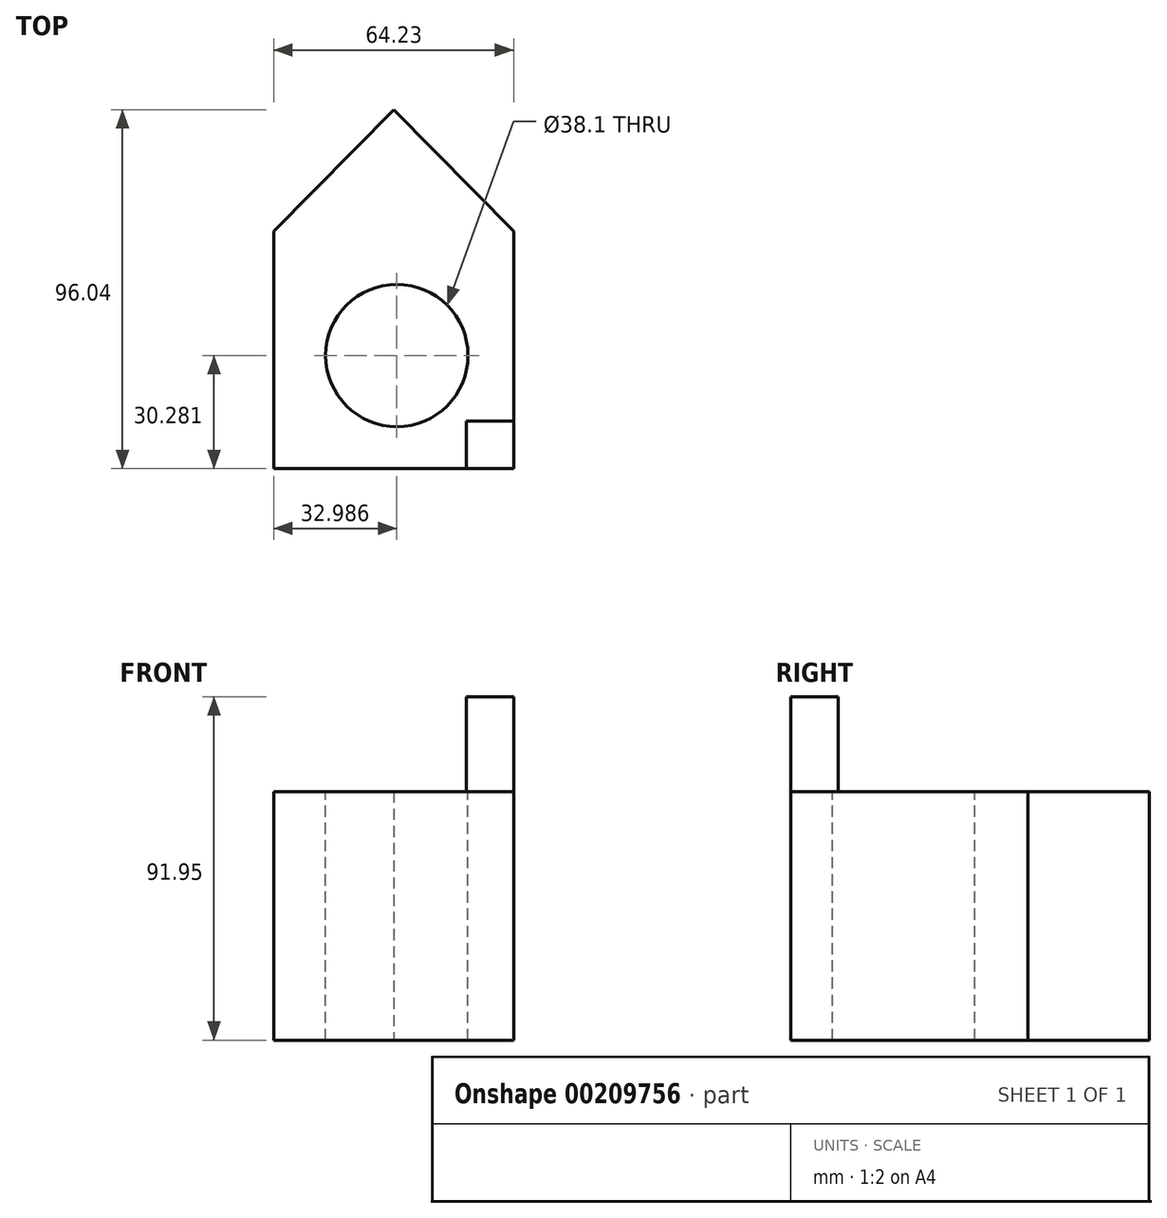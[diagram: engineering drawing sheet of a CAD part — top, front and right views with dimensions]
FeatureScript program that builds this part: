
annotation { "Feature Type Name" : "Feature", "Feature Type Description" : "" }
export const myFeature = defineFeature(function(context is Context, id is Id, definition is map)
    precondition{}
    {
        {
            var Q0;
            Q0=qCreatedBy(makeId("Top.planeOp"),FACE);
            var sketch = newSketch(context, id + "F0", { "sketchPlane" : qUnion([Q0])});
            skLineSegment(sketch, "E0.bottom", {"start": v(0, 0) * mm, "end": v(64.23, 0) * mm});
            skLineSegment(sketch, "E0.top", {"start": v(0, 63.5) * mm, "end": v(64.23, 63.5) * mm});
            skLineSegment(sketch, "E0.left", {"start": v(0, 0) * mm, "end": v(0, 63.5) * mm});
            skLineSegment(sketch, "E0.right", {"start": v(64.23, 0) * mm, "end": v(64.23, 63.5) * mm});
            skLineSegment(sketch, "E1", {"start": v(0, 63.5) * mm, "end": v(32.12, 96.04) * mm});
            skPoint(sketch, "E1.endSnap0", {"position": v(32.12, 63.5) * mm});
            skLineSegment(sketch, "E2", {"start": v(64.23, 63.5) * mm, "end": v(32.12, 96.04) * mm});
            skSolve(sketch);
        }
        {
            var Q0;
            Q0 = qSketchRegion(id + "F0", true);
            extrude(context, id + "F1", {"entities" : qUnion([Q0]), "depth" : 66.55 * mm});
        }
        {
            var Q0;
            Q0=makeQuery(id+"F1.opExtrude","CAP_FACE",FACE,{"disambiguationData":[OSD([sQuery(id+"F0.wireOp",EDGE,"E0.bottom"),sQuery(id+"F0.wireOp",EDGE,"E0.left"),sQuery(id+"F0.wireOp",EDGE,"E0.right"),sQuery(id+"F0.wireOp",EDGE,"E1"),sQuery(id+"F0.wireOp",EDGE,"E2")])],"isStart":false});
            var sketch = newSketch(context, id + "F2", { "sketchPlane" : qUnion([Q0])});
            skCircle(sketch, "E3", {"center": v(32.99, 30.28) * mm, "radius": 19.05 * mm});
            skSolve(sketch);
        }
        {
            var Q0;
            Q0 = qSketchRegion(id + "F2", true);
            extrude(context, id + "F3", {"entities" : qUnion([Q0]), "operationType" : NewBodyOperationType.REMOVE, "endBound" : BoundingType.THROUGH_ALL, "oppositeDirection" : true, "depth" : 25.4 * mm});
        }
        {
            var Q0;
            Q0=makeQuery(id+"F1.opExtrude","CAP_FACE",FACE,{"disambiguationData":[OSD([sQuery(id+"F0.wireOp",EDGE,"E0.bottom"),sQuery(id+"F0.wireOp",EDGE,"E0.left"),sQuery(id+"F0.wireOp",EDGE,"E0.right"),sQuery(id+"F0.wireOp",EDGE,"E1"),sQuery(id+"F0.wireOp",EDGE,"E2")])],"isStart":false});
            var sketch = newSketch(context, id + "F4", { "sketchPlane" : qUnion([Q0])});
            skLineSegment(sketch, "E4.bottom", {"start": v(51.53, 12.7) * mm, "end": v(64.23, 12.7) * mm});
            skLineSegment(sketch, "E4.top", {"start": v(51.53, 0) * mm, "end": v(64.23, 0) * mm});
            skLineSegment(sketch, "E4.left", {"start": v(51.53, 12.7) * mm, "end": v(51.53, 0) * mm});
            skLineSegment(sketch, "E4.right", {"start": v(64.23, 12.7) * mm, "end": v(64.23, 0) * mm});
            skSolve(sketch);
        }
        {
            var Q0;
            Q0=makeQuery(id+"F4.imprint","IMPRINT",FACE,{"disambiguationData":[TD([[makeQuery(id+"F4.imprint","IMPRINT",EDGE,{"derivedFrom":sQuery(id+"F4.wireOp",EDGE,"E4.bottom")}),-1.0]])]});
            extrude(context, id + "F5", {"entities" : qUnion([Q0]), "depth" : 25.4 * mm});
        }
    });
